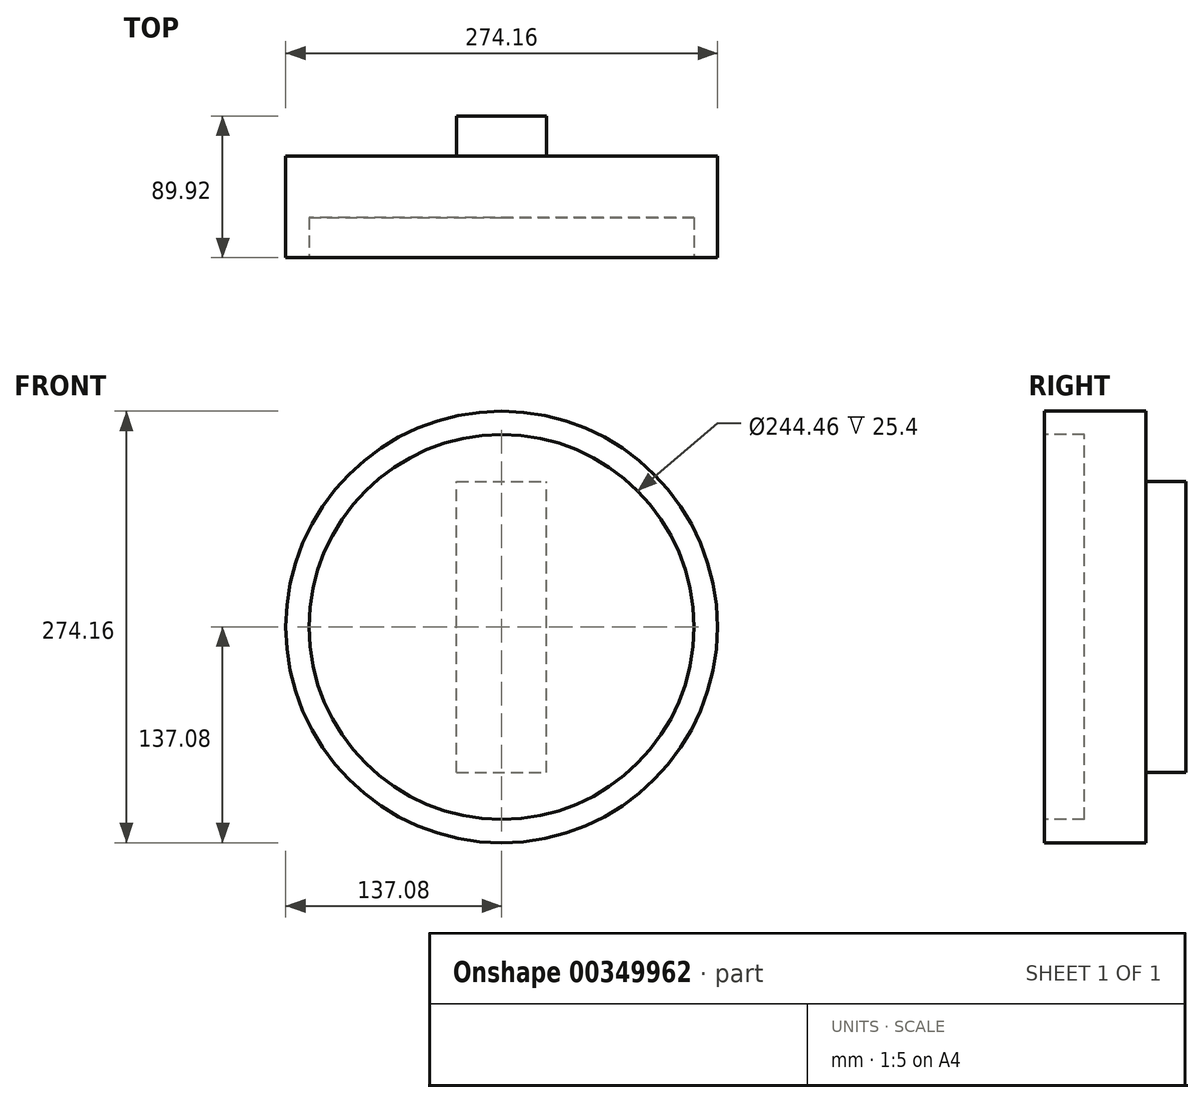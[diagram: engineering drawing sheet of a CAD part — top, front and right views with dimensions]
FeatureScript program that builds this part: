
annotation { "Feature Type Name" : "Feature", "Feature Type Description" : "" }
export const myFeature = defineFeature(function(context is Context, id is Id, definition is map)
    precondition{}
    {
        {
            var Q0;
            Q0=qCreatedBy(makeId("Front.planeOp"),FACE);
            var sketch = newSketch(context, id + "F0", { "sketchPlane" : qUnion([Q0])});
            skCircle(sketch, "E0", {"center": v(0, 0) * mm, "radius": 137.08 * mm});
            skSolve(sketch);
        }
        {
            var Q0;
            Q0 = qSketchRegion(id + "F0", true);
            extrude(context, id + "F1", {"entities" : qUnion([Q0]), "depth" : 64.52 * mm});
        }
        {
            var Q0;
            Q0=makeQuery(id+"F1.opExtrude","CAP_FACE",FACE,{"disambiguationData":[OSD([sQuery(id+"F0.wireOp",EDGE,"E0")])],"isStart":false});
            var sketch = newSketch(context, id + "F2", { "sketchPlane" : qUnion([Q0])});
            skCircle(sketch, "E1", {"center": v(0, 0) * mm, "radius": 122.23 * mm});
            skSolve(sketch);
        }
        {
            var Q0;
            Q0 = qSketchRegion(id + "F2", true);
            extrude(context, id + "F3", {"entities" : qUnion([Q0]), "operationType" : NewBodyOperationType.REMOVE, "oppositeDirection" : true, "depth" : 25.4 * mm});
        }
        {
            var Q0;
            Q0=makeQuery(id+"F1.opExtrude","CAP_FACE",FACE,{"disambiguationData":[OSD([sQuery(id+"F0.wireOp",EDGE,"E0")])],"isStart":true});
            var sketch = newSketch(context, id + "F4", { "sketchPlane" : qUnion([Q0])});
            skLineSegment(sketch, "E2.bottom", {"start": v(28.5, -92.53) * mm, "end": v(-28.5, -92.53) * mm});
            skLineSegment(sketch, "E2.top", {"start": v(28.5, 92.53) * mm, "end": v(-28.5, 92.53) * mm});
            skLineSegment(sketch, "E2.left", {"start": v(28.5, -92.53) * mm, "end": v(28.5, 92.53) * mm});
            skLineSegment(sketch, "E2.right", {"start": v(-28.5, -92.53) * mm, "end": v(-28.5, 92.53) * mm});
            skPoint(sketch, "E2.middle", {"position": v(0, 0) * mm});
            skSolve(sketch);
        }
        {
            var Q0;
            Q0 = qSketchRegion(id + "F4", true);
            extrude(context, id + "F5", {"entities" : qUnion([Q0]), "operationType" : NewBodyOperationType.ADD, "depth" : 25.4 * mm});
        }
    });
